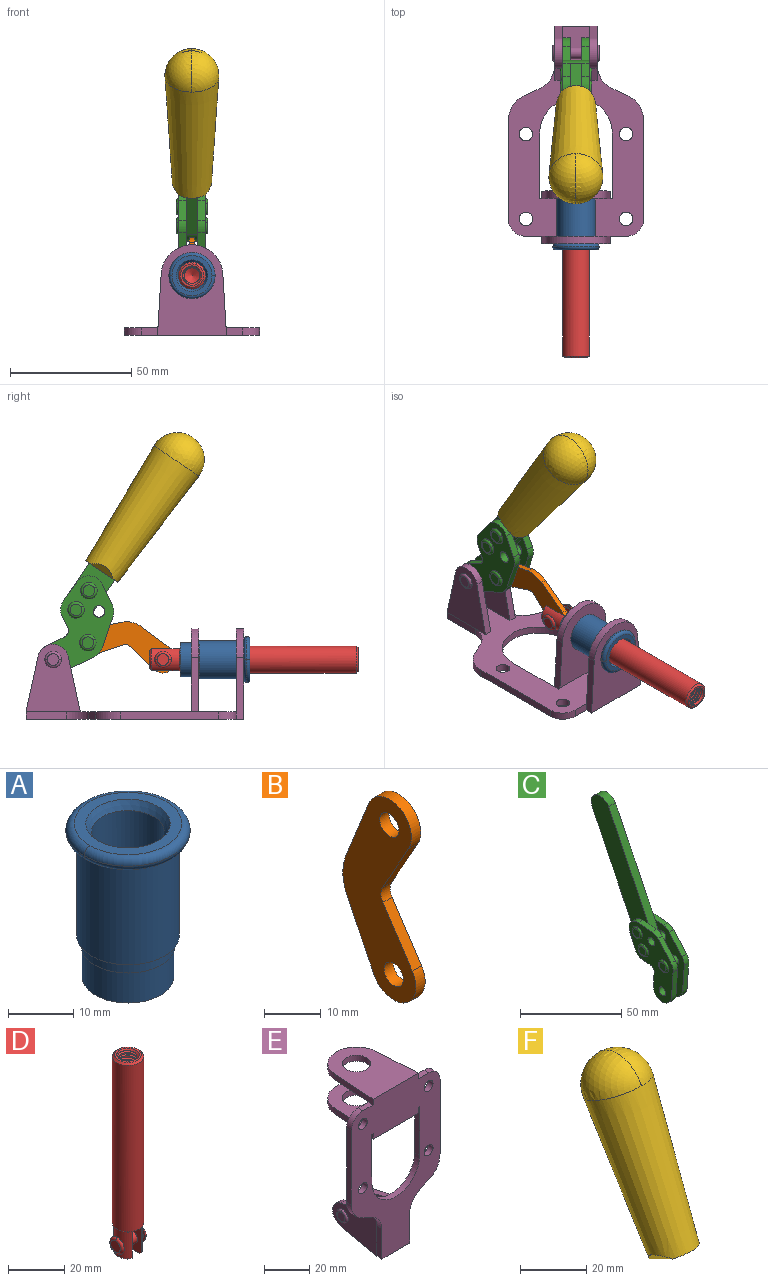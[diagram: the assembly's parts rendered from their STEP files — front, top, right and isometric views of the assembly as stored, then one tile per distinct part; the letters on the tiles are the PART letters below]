
ASSEMBLY  parts=6 mates=6
PART A: 15 faces, bbox 20.6x20.6x28.7 mm
  f0: torus R=8.26mm, axis (0,0,1), area 56.8mm2, adj f1,f10,f12
  f1: torus R=8.26mm, axis (0,0,1), area 56.8mm2, adj f0,f6,f13
  f2: cylinder r=5.59mm len=25.91mm, axis (0,0,1), area 909.6mm2, adj f3,f4
  f3: cone r=6.86mm half-angle=45deg, axis (0,0,-1), area 70.2mm2, adj f2,f14
  f4: cone r=6.47mm half-angle=30deg, axis (0,0,1), area 66.7mm2, adj f2,f13
  f5: cylinder r=7.04mm len=14.07mm, axis (0,0,1), area 252.6mm2, adj f11,f14
  f6: torus R=8.26mm, axis (0,0,1), area 56.8mm2, adj f1,f12,f13
  f7: cylinder r=7.16mm len=14.33mm, axis (0,0,1), area 91.5mm2, adj f9,f11
  f8: cylinder r=7.86mm len=18.42mm, axis (0,0,1), area 909.6mm2, adj f9,f10
  f9: plane 15.72x15.72mm, normal (0,0,-1), area 33mm2, adj f7,f8
  f10: plane 16.51x16.51mm, normal (0,0,-1), area 19.9mm2, adj f0,f8,f12
  f11: plane 14.33x14.33mm, normal (0,0,-1), area 5.7mm2, adj f5,f7
  f12: torus R=8.26mm, axis (0,0,1), area 56.8mm2, adj f0,f6,f10
  f13: plane 16.51x16.51mm, normal (0,0,1), area 82.7mm2, adj f1,f4,f6
  f14: plane 14.07x14.07mm, normal (0,0,-1), area 7.8mm2, adj f3,f5
PART B: 12 faces, bbox 2.3x18.2x42.8 mm
  f0: cylinder r=2.4mm len=4.8mm, axis (1,0,0), area 34.9mm2, adj f4,f11
  f1: cylinder r=10.41mm len=8.47mm, axis (1,0,0), area 20.2mm2, adj f4,f9,f10,f11
  f2: cylinder r=3.05mm len=3.16mm, axis (1,0,0), area 7.7mm2, adj f4,f6,f7,f11
  f3: cylinder r=2.4mm len=4.8mm, axis (1,0,0), area 34.9mm2, adj f4,f11
  f4: plane 42.81x18.23mm, normal (-1,0,0), area 414.1mm2, adj f0,f1,f2,f3,f5,f6,f7,f8
  f5: cylinder r=5.54mm len=10.67mm, axis (1,0,0), area 41.8mm2, adj f4,f6,f10,f11
  f6: plane 11.66x6.53mm, normal (0,-0.87,-0.49), area 30.9mm2, adj f2,f4,f5,f11
  f7: plane 11.17x7.33mm, normal (0,-0.84,0.55), area 30.9mm2, adj f2,f4,f8,f11
  f8: cylinder r=5.54mm len=10.51mm, axis (1,0,0), area 41.8mm2, adj f4,f7,f9,f11
  f9: plane 13.67x6.67mm, normal (0,0.9,-0.44), area 35.1mm2, adj f1,f4,f8,f11
  f10: plane 14.1x5.7mm, normal (0,0.93,0.37), area 35.1mm2, adj f1,f4,f5,f11
  f11: plane 42.81x18.23mm, normal (1,0,0), area 414.1mm2, adj f0,f1,f2,f3,f5,f6,f7,f8
PART C: 59 faces, bbox 12.9x60.2x99.6 mm
  f0: torus R=2.39mm, axis (-1,0,0), area 14.9mm2, adj f20,f43,f51
  f1: torus R=2.39mm, axis (-1,0,0), area 14.9mm2, adj f19,f42,f51
  f2: torus R=2.39mm, axis (-1,0,0), area 14.9mm2, adj f18,f35,f51
  f3: torus R=2.39mm, axis (-1,0,0), area 14.9mm2, adj f14,f17,f23
  f4: torus R=2.39mm, axis (-1,0,0), area 14.9mm2, adj f13,f16,f23
  f5: torus R=2.39mm, axis (-1,0,0), area 14.9mm2, adj f12,f15,f23
  f6: cylinder r=2.39mm len=4.78mm, axis (1,0,0), area 46.5mm2, adj f48,f50,f51
  f7: cylinder r=2.39mm len=4.78mm, axis (1,0,0), area 46.5mm2, adj f50,f51
  f8: cylinder r=6.35mm len=12.68mm, axis (1,0,0), area 61.8mm2, adj f38,f39,f50,f51
  f9: cylinder r=2.39mm len=4.78mm, axis (-1,0,0), area 70.5mm2, adj f46,f50
  f10: cylinder r=2.39mm len=4.78mm, axis (-1,0,0), area 46.5mm2, adj f23,f45,f46
  f11: cylinder r=2.39mm len=4.78mm, axis (-1,0,0), area 46.5mm2, adj f23,f46
  f12: plane 4.78x4.78mm, normal (1,0,0), area 17.9mm2, adj f5,f15
  f13: plane 4.78x4.78mm, normal (1,0,0), area 17.9mm2, adj f4,f16
  f14: plane 4.78x4.78mm, normal (1,0,0), area 17.9mm2, adj f3,f17
  f15: torus R=2.39mm, axis (-1,0,0), area 14.9mm2, adj f5,f12,f23
  f16: torus R=2.39mm, axis (-1,0,0), area 14.9mm2, adj f4,f13,f23
  f17: torus R=2.39mm, axis (-1,0,0), area 14.9mm2, adj f3,f14,f23
  f18: plane 4.78x4.78mm, normal (-1,0,0), area 17.9mm2, adj f2,f35
  f19: plane 4.78x4.78mm, normal (-1,0,0), area 17.9mm2, adj f1,f42
  f20: plane 4.78x4.78mm, normal (-1,0,0), area 17.9mm2, adj f0,f43
  f21: plane 2.26x0.2mm, normal (1,0,0), area 0.2mm2, adj f31,f44
  f22: plane 2.26x0.2mm, normal (-1,0,0), area 0.2mm2, adj f41,f44
  f23: plane 39.37x30.77mm, normal (1,0,0), area 565.5mm2, adj f3,f4,f5,f10,f11,f15,f16,f17
  f24: cylinder r=6.1mm len=4.15mm, axis (-1,0,0), area 14.7mm2, adj f23,f25,f32,f46
  f25: plane 10.25x9.01mm, normal (0,-0.75,0.66), area 42.3mm2, adj f23,f24,f26,f46
  f26: cylinder r=6.35mm len=4.64mm, axis (-1,0,0), area 15.6mm2, adj f23,f25,f27,f46
  f27: plane 15.84x3.1mm, normal (0,-1,-0.07), area 49.2mm2, adj f23,f26,f28,f46
  f28: cylinder r=6.35mm len=12.68mm, axis (-1,0,0), area 61.8mm2, adj f23,f27,f29,f46
  f29: plane 8.11x3.1mm, normal (0,1,0.07), area 25.2mm2, adj f23,f28,f30,f46
  f30: cylinder r=3.05mm len=3.25mm, axis (-1,0,0), area 14.8mm2, adj f23,f29,f31,f46
  f31: plane 5.99x3.1mm, normal (0,0.07,-1), area 18.6mm2, adj f21,f23,f30,f44,f46
  f32: plane 9.5x3.1mm, normal (0,-0.07,1), area 29.5mm2, adj f23,f24,f33,f46,f47
  f33: cylinder r=6.1mm len=8.63mm, axis (-1,0,0), area 39.1mm2, adj f23,f32,f34,f47
  f34: plane 8.65x3.96mm, normal (0,0.91,-0.42), area 29.5mm2, adj f23,f33,f44,f47
  f35: torus R=2.39mm, axis (-1,0,0), area 14.9mm2, adj f2,f18,f51
  f36: plane 10.25x9.01mm, normal (0,-0.75,0.66), area 42.3mm2, adj f37,f49,f50,f51
  f37: cylinder r=6.35mm len=4.64mm, axis (1,0,0), area 15.6mm2, adj f36,f38,f50,f51
  f38: plane 15.84x3.1mm, normal (0,-1,-0.07), area 49.2mm2, adj f8,f37,f50,f51
  f39: plane 8.11x3.1mm, normal (0,1,0.07), area 25.2mm2, adj f8,f40,f50,f51
  f40: cylinder r=3.05mm len=3.25mm, axis (1,0,0), area 14.8mm2, adj f39,f41,f50,f51
  f41: plane 5.99x3.1mm, normal (0,0.07,-1), area 18.6mm2, adj f22,f40,f44,f50,f51
  f42: torus R=2.39mm, axis (-1,0,0), area 14.9mm2, adj f1,f19,f51
  f43: torus R=2.39mm, axis (-1,0,0), area 14.9mm2, adj f0,f20,f51
  f44: cylinder r=6.35mm len=12.12mm, axis (-1,0,0), area 128.9mm2, adj f21,f22,f23,f31,f34,f41,f46,f47
  f45: plane 2.65x1.35mm, normal (1,0,0), area 1mm2, adj f10,f55
  f46: plane 39.08x20.42mm, normal (-1,0,0), area 412.5mm2, adj f9,f10,f11,f24,f25,f26,f27,f28
  f47: plane 77.62x39.82mm, normal (1,0,0), area 850mm2, adj f32,f33,f34,f44,f53,f54,f55
  f48: plane 2.65x1.35mm, normal (-1,0,0), area 1mm2, adj f6,f55
  f49: cylinder r=6.1mm len=4.15mm, axis (1,0,0), area 14.7mm2, adj f36,f50,f51,f56
  f50: plane 39.08x20.42mm, normal (1,0,0), area 412.5mm2, adj f6,f7,f8,f9,f36,f37,f38,f39
  f51: plane 39.37x30.77mm, normal (-1,0,0), area 565.5mm2, adj f0,f1,f2,f6,f7,f8,f35,f36
  f52: plane 8.65x3.96mm, normal (0,0.91,-0.42), area 29.5mm2, adj f44,f51,f57,f58
  f53: plane 68.49x33.4mm, normal (0,0.9,-0.44), area 358.1mm2, adj f44,f47,f54,f58
  f54: cylinder r=6.35mm len=12.06mm, axis (1,0,0), area 93.7mm2, adj f47,f53,f55,f58
  f55: plane 68.49x33.4mm, normal (0,-0.9,0.44), area 358.1mm2, adj f44,f45,f46,f47,f48,f50,f54,f58
  f56: plane 9.5x3.1mm, normal (0,-0.07,1), area 29.5mm2, adj f49,f50,f51,f57,f58
  f57: cylinder r=6.1mm len=8.63mm, axis (1,0,0), area 39.1mm2, adj f51,f52,f56,f58
  f58: plane 77.62x39.82mm, normal (-1,0,0), area 850mm2, adj f44,f52,f53,f54,f55,f56,f57
PART D: 48 faces, bbox 12.6x11.1x86.1 mm
  f0: torus R=2.41mm, axis (-1,0,0), area 15mm2, adj f30,f32,f34
  f1: torus R=2.41mm, axis (-1,0,0), area 15mm2, adj f29,f31,f33
  f2: cylinder r=5.54mm len=72.39mm, axis (0,0,1), area 2518.5mm2, adj f3,f4,f42,f43
  f3: cone r=5.54mm half-angle=45deg, axis (0,0,1), area 7.6mm2, adj f2,f5,f41
  f4: cone r=5.54mm half-angle=45deg, axis (0,0,-1), area 34.9mm2, adj f2,f39
  f5: cylinder r=5.08mm len=11.48mm, axis (0,0,1), area 108.3mm2, adj f3,f7,f8,f41
  f6: cylinder r=2.41mm len=4.83mm, axis (-1,0,0), area 71.2mm2, adj f40,f41
  f7: cylinder r=2.41mm len=4.83mm, axis (-1,0,0), area 7.6mm2, adj f5,f34
  f8: cone r=5.08mm half-angle=45deg, axis (0,0,1), area 10.6mm2, adj f5,f37,f41
  f9: cone r=3.98mm half-angle=45deg, axis (0,0,1), area 17.6mm2, adj f27,f39,f45,f46,f47
  f10: cylinder r=2.41mm len=4.83mm, axis (-1,0,0), area 7.6mm2, adj f33,f38
  f11: cylinder r=3.2mm len=6.4mm, axis (0,0,1), area 78.4mm2, adj f12,f28,f44,f45,f47
  f12: cylinder r=3.2mm len=6.4mm, axis (0,0,1), area 10.5mm2, adj f11,f13,f45,f47
  f13: cylinder r=3.2mm len=6.4mm, axis (0,0,1), area 10.5mm2, adj f12,f14,f45,f47
  f14: cylinder r=3.2mm len=6.4mm, axis (0,0,1), area 10.5mm2, adj f13,f15,f45,f47
  f15: cylinder r=3.2mm len=6.4mm, axis (0,0,1), area 10.5mm2, adj f14,f16,f45,f47
  f16: cylinder r=3.2mm len=6.4mm, axis (0,0,1), area 10.5mm2, adj f15,f17,f45,f47
  f17: cylinder r=3.2mm len=6.4mm, axis (0,0,1), area 10.5mm2, adj f16,f18,f45,f47
  f18: cylinder r=3.2mm len=6.4mm, axis (0,0,1), area 10.5mm2, adj f17,f19,f45,f47
  f19: cylinder r=3.2mm len=6.4mm, axis (0,0,1), area 10.5mm2, adj f18,f20,f45,f47
  f20: cylinder r=3.2mm len=6.4mm, axis (0,0,1), area 10.5mm2, adj f19,f21,f45,f47
  f21: cylinder r=3.2mm len=6.4mm, axis (0,0,1), area 10.5mm2, adj f20,f22,f45,f47
  f22: cylinder r=3.2mm len=6.4mm, axis (0,0,1), area 10.5mm2, adj f21,f23,f45,f47
  f23: cylinder r=3.2mm len=6.4mm, axis (0,0,1), area 10.5mm2, adj f22,f24,f45,f47
  f24: cylinder r=3.2mm len=6.4mm, axis (0,0,1), area 10.5mm2, adj f23,f25,f45,f47
  f25: cylinder r=3.2mm len=6.4mm, axis (0,0,1), area 10.5mm2, adj f24,f26,f45,f47
  f26: cylinder r=3.2mm len=6.4mm, axis (0,0,1), area 10.5mm2, adj f25,f27,f45,f47
  f27: cylinder r=3.2mm len=6.4mm, axis (0,0,1), area 7.4mm2, adj f9,f26,f45,f47
  f28: cone r=3.2mm half-angle=60deg, axis (0,0,1), area 37.2mm2, adj f11
  f29: plane 4.83x4.83mm, normal (-1,0,0), area 18.3mm2, adj f1,f31
  f30: plane 4.83x4.83mm, normal (1,0,0), area 18.3mm2, adj f0,f32
  f31: torus R=2.41mm, axis (-1,0,0), area 15mm2, adj f1,f29,f33
  f32: torus R=2.41mm, axis (-1,0,0), area 15mm2, adj f0,f30,f34
  f33: plane 6.83x6.83mm, normal (1,0,0), area 18.3mm2, adj f1,f10,f31
  f34: plane 6.83x6.83mm, normal (-1,0,0), area 18.3mm2, adj f0,f7,f32
  f35: cone r=5.08mm half-angle=45deg, axis (0,0,1), area 10.6mm2, adj f36,f38,f40
  f36: plane 7.25x1.97mm, normal (0,0,-1), area 10mm2, adj f35,f40
  f37: plane 7.25x1.97mm, normal (0,0,-1), area 10mm2, adj f8,f41
  f38: cylinder r=5.08mm len=11.48mm, axis (0,0,1), area 108.3mm2, adj f10,f35,f40,f42
  f39: plane 9.55x9.55mm, normal (0,0,1), area 22mm2, adj f4,f9
  f40: plane 12.76x10.09mm, normal (1,0,0), area 95.7mm2, adj f6,f35,f36,f38,f42,f43
  f41: plane 12.76x10.09mm, normal (-1,0,0), area 95.7mm2, adj f3,f5,f6,f8,f37,f43
  f42: cone r=5.54mm half-angle=45deg, axis (0,0,1), area 7.6mm2, adj f2,f38,f40
  f43: plane 11.07x4.7mm, normal (0,0,-1), area 50.4mm2, adj f2,f40,f41
  f44: plane 0.89x0.62mm, normal (-1,0,0), area 0.3mm2, adj f11,f45,f46,f47
  f45: bspline ~24.8x7.63mm, area 266.6mm2, adj f9,f11,f12,f13,f14,f15,f16,f17
  f46: bspline ~24.87x7.63mm, area 73.6mm2, adj f9,f44,f45,f47
  f47: bspline ~24.98x7.63mm, area 272.5mm2, adj f9,f11,f12,f13,f14,f15,f16,f17
PART E: 55 faces, bbox 55.7x37.4x89.8 mm
  f0: torus R=2.41mm, axis (-1,0,0), area 15mm2, adj f11,f15,f25
  f1: torus R=2.41mm, axis (-1,0,0), area 15mm2, adj f10,f12,f22
  f2: cylinder r=2.78mm len=5.56mm, axis (0,-1,0), area 54.2mm2, adj f30,f54
  f3: cylinder r=14.99mm len=29.97mm, axis (0,-1,0), area 145.9mm2, adj f30,f49,f53,f54
  f4: cylinder r=2.78mm len=5.56mm, axis (0,-1,0), area 54.2mm2, adj f30,f54
  f5: cylinder r=2.78mm len=5.56mm, axis (0,-1,0), area 54.2mm2, adj f30,f54
  f6: cylinder r=2.78mm len=5.56mm, axis (0,-1,0), area 54.2mm2, adj f30,f54
  f7: cylinder r=6.35mm len=12.7mm, axis (0,0,1), area 123.6mm2, adj f27,f51
  f8: cylinder r=6.35mm len=12.7mm, axis (0,0,-1), area 124.7mm2, adj f21,f35
  f9: cylinder r=2.41mm len=11.18mm, axis (-1,0,0), area 169.4mm2, adj f16,f19
  f10: plane 4.83x4.83mm, normal (1,0,0), area 18.3mm2, adj f1,f12
  f11: plane 4.83x4.83mm, normal (-1,0,0), area 18.3mm2, adj f0,f15
  f12: torus R=2.41mm, axis (-1,0,0), area 15mm2, adj f1,f10,f22
  f13: cylinder r=6.35mm len=12.41mm, axis (1,0,0), area 53.4mm2, adj f18,f19,f22,f23
  f14: cylinder r=6.35mm len=12.41mm, axis (-1,0,0), area 53.4mm2, adj f16,f17,f24,f25
  f15: torus R=2.41mm, axis (-1,0,0), area 15mm2, adj f0,f11,f25
  f16: plane 27.86x22.35mm, normal (1,0,0), area 425.4mm2, adj f9,f14,f17,f24,f30
  f17: plane 22.86x4.97mm, normal (0,0.21,0.98), area 72.5mm2, adj f14,f16,f25,f30
  f18: plane 22.86x4.97mm, normal (0,0.21,0.98), area 72.5mm2, adj f13,f19,f22,f30
  f19: plane 27.86x22.35mm, normal (-1,0,0), area 425.4mm2, adj f9,f13,f18,f23,f30
  f20: cylinder r=12.7mm len=25.35mm, axis (0,0,-1), area 119.8mm2, adj f21,f34,f35,f36
  f21: plane 34.21x28.07mm, normal (0,0,-1), area 702.4mm2, adj f8,f20,f30,f34,f36
  f22: plane 27.96x22.45mm, normal (1,0,0), area 407.2mm2, adj f1,f12,f13,f18,f23,f30,f42,f43
  f23: plane 22.86x4.97mm, normal (0,0.21,-0.98), area 72.5mm2, adj f13,f19,f22,f44
  f24: plane 22.86x4.97mm, normal (0,0.21,-0.98), area 72.5mm2, adj f14,f16,f25,f44
  f25: plane 27.86x22.35mm, normal (-1,0,0), area 407.1mm2, adj f0,f14,f15,f17,f24,f30,f45,f46
  f26: plane 3.1x0.95mm, normal (0,0,-1), area 2.7mm2, adj f30,f49,f50,f54
  f27: plane 34.21x28.07mm, normal (0,0,1), area 702.4mm2, adj f7,f28,f30,f50,f52
  f28: cylinder r=12.7mm len=25.35mm, axis (0,0,1), area 118.8mm2, adj f27,f50,f51,f52
  f29: plane 3.1x0.95mm, normal (0,0,-1), area 2.7mm2, adj f30,f52,f53,f54
  f30: plane 86.54x55.63mm, normal (0,1,0), area 2362.9mm2, adj f2,f3,f4,f5,f6,f16,f17,f18
  f31: plane 40.56x3.1mm, normal (-1,0,0), area 125.7mm2, adj f30,f32,f48,f54
  f32: cylinder r=7.11mm len=7.11mm, axis (0,-1,0), area 34.6mm2, adj f30,f31,f33,f54
  f33: plane 6.67x3.1mm, normal (0,0,1), area 20.4mm2, adj f30,f32,f34,f54
  f34: plane 25.39x3.13mm, normal (-1,0.06,0), area 79.5mm2, adj f20,f21,f33,f35,f54
  f35: plane 37.31x28.45mm, normal (0,0,1), area 789.9mm2, adj f8,f20,f34,f36,f54
  f36: plane 25.39x3.13mm, normal (1,0.06,0), area 79.5mm2, adj f20,f21,f35,f37,f54
  f37: plane 6.67x3.1mm, normal (0,0,1), area 20.4mm2, adj f30,f36,f38,f54
  f38: cylinder r=7.11mm len=7.11mm, axis (0,-1,0), area 34.6mm2, adj f30,f37,f39,f54
  f39: plane 40.56x3.1mm, normal (1,0,0), area 125.7mm2, adj f30,f38,f40,f54
  f40: cylinder r=11.18mm len=10.16mm, axis (0,-1,0), area 39.5mm2, adj f30,f39,f41,f54
  f41: plane 6.09x3.1mm, normal (0.42,0,-0.91), area 20.8mm2, adj f30,f40,f42,f54
  f42: cylinder r=11.18mm len=9.41mm, axis (0,-1,0), area 37.2mm2, adj f22,f30,f41,f43,f54
  f43: plane 16.5x3.1mm, normal (1,0,0), area 51.1mm2, adj f22,f42,f44,f54
  f44: plane 17.37x3.1mm, normal (0,0,-1), area 53.8mm2, adj f23,f24,f30,f43,f45,f54
  f45: plane 16.5x3.1mm, normal (-1,0,0), area 51.1mm2, adj f25,f44,f46,f54
  f46: cylinder r=11.18mm len=9.41mm, axis (0,-1,0), area 37.2mm2, adj f25,f30,f45,f47,f54
  f47: plane 6.09x3.1mm, normal (-0.42,0,-0.91), area 20.8mm2, adj f30,f46,f48,f54
  f48: cylinder r=11.18mm len=10.16mm, axis (0,-1,0), area 39.5mm2, adj f30,f31,f47,f54
  f49: plane 26.54x3.1mm, normal (-1,0,0), area 82.3mm2, adj f3,f26,f30,f54
  f50: plane 25.39x3.1mm, normal (1,0.06,0), area 78.8mm2, adj f26,f27,f28,f51,f54
  f51: plane 37.31x28.45mm, normal (0,0,-1), area 789.9mm2, adj f7,f28,f50,f52,f54
  f52: plane 25.39x3.1mm, normal (-1,0.06,0), area 78.8mm2, adj f27,f28,f29,f51,f54
  f53: plane 26.54x3.1mm, normal (1,0,0), area 82.3mm2, adj f3,f29,f30,f54
  f54: plane 89.66x55.63mm, normal (0,-1,0), area 2678.5mm2, adj f2,f3,f4,f5,f6,f26,f29,f31
PART F: 11 faces, bbox 22.3x42.6x64.5 mm
  f0: sphere r=11.13mm, area 411.4mm2, adj f1,f8
  f1: cone r=11.11mm half-angle=3.3deg, axis (0,0.44,0.9), area 3251.8mm2, adj f0,f7,f8,f9,f10
  f2: cylinder r=6.16mm len=11.7mm, axis (1,0,0), area 89.5mm2, adj f3,f4,f5,f6
  f3: plane 60.23x36.75mm, normal (-1,0,0), area 763.6mm2, adj f2,f4,f6,f10
  f4: plane 51.37x25.05mm, normal (0,0.9,-0.44), area 264.2mm2, adj f2,f3,f5,f10
  f5: plane 60.23x36.75mm, normal (1,0,0), area 763.6mm2, adj f2,f4,f6,f10
  f6: plane 51.37x25.05mm, normal (0,-0.9,0.44), area 264.2mm2, adj f2,f3,f5,f10
  f7: plane 9.95x5.95mm, normal (0.71,-0.31,-0.64), area 25.8mm2, adj f1,f10
  f8: sphere r=11.13mm, area 411.4mm2, adj f0,f1
  f9: plane 9.95x5.95mm, normal (-0.71,-0.31,-0.64), area 25.8mm2, adj f1,f10
  f10: plane 14.27x11.38mm, normal (0,-0.44,-0.9), area 106.7mm2, adj f1,f3,f4,f5,f6,f7,f9
PLACE A rot(axis=(1,0,0),90deg) t=(0,1.23,0)mm
PLACE B rot(axis=(1,0,0),104.7deg) t=(0,9.28,4.72)mm
PLACE C rot(axis=(1,0,0),60deg) t=(0,-6.77,19.34)mm
PLACE D rot(axis=(1,0,0),90deg) t=(0,3.55,0)mm
PLACE E rot(axis=(1,0,0),90deg) t=(0,1.23,0)mm fixed
PLACE F rot(axis=(1,0,0),60deg) t=(-0.04,-6.77,19.34)mm
MATE revolute B.f3 <-> C.f4  axis (1,0,0) through (0,19.06,31.57)mm
MATE slider D.f2 <-> E.f7  axis (0,-1,0) through (0,-55.23,24.61)mm
MATE revolute C.f7 <-> E.f0  axis (1,0,0) through (0,33.32,24.61)mm
MATE fastened A.f2 <-> E.f7  axis (0,1,0) through (0,-45.16,24.61)mm
MATE revolute B.f5 <-> D.f6  axis (1,0,0) through (0,-11.92,24.61)mm
MATE fastened F.f2 <-> C.f54  axis (1,0,0) through (-2.35,-18.69,108.25)mm
